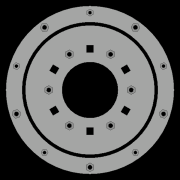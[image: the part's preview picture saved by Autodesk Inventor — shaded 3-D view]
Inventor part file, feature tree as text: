
AUTODESK INVENTOR PART (.ipt)
format: ipt  version: 2022.2 (Build 262287010, 287A)  size: 832,512 bytes
history: native  units: mm
features: extrude x28, other x19, sketch x17, pattern_circular x11, plane x4, fillet x2, move_body x2, revolve x2, draft x2, chamfer x2
ambient origin geometry x8: Origin, YZ Plane, XZ Plane, XY Plane, X Axis, Y Axis, Z Axis, Center Point
bodies: Solid5 (feature_tree)
feature tree (89):
  other  "CrossSection1"
  sketch  "Sketch7"  dims[d167=8.972256mm]
  other  "Roller1"
  other  "Roller2"
  sketch  "Sketch22"  dims[d173=10.814812mm]
  sketch  "Sketch2"  dims[d57=4.025mm d90=61.984365mm]
  sketch  "Sketch23"  dims[d201=75.0mm d232=0.0mm d233=3600.0mm]
  other  "RevRoller1"
  fillet  "Fillet1"  Radius=59.246882mm
  extrude  "Extrusion39"  Depth=61.984365mm
  pattern_circular  "Circular Pattern13"  Count=360  [1 undecoded]
  move_body  "Move Body7"
  revolve  "Revolution13"  [1 undecoded]
  fillet  "Fillet3"  Radius=0.025mm
  pattern_circular  "Circular Pattern14"  Count=24  [1 undecoded]
  move_body  "Move Body6"
  revolve  "Revolution14"  Angle=360.0deg
  other  "OuterRim_Top2"
  other  "OuterRim_Bottom2"
  plane  "Work Plane8"
  sketch  "Sketch49"  dims[d352=0.025mm]
  sketch  "Sketch50"  dims[d354=0.025mm]
  sketch  "Sketch51"  dims[d355=16.1595mm]
  extrude  "Extrusion40"  Depth=0.75mm
  extrude  "Extrusion41"  Depth=0.75mm
  extrude  "Extrusion42"  Depth=0.75mm
  extrude  "Extrusion43"  Depth=1.0mm
  sketch  "Sketch52"  dims[d356=16.159664mm]
  extrude  "Extrusion44"  Depth=0.75mm
  extrude  "Extrusion45"  TaperAngle=90.0deg  [1 undecoded]
  extrude  "Extrusion46"  Depth=0.75mm
  extrude  "Extrusion47"  Depth=0.75mm
  pattern_circular  "Circular Pattern32"  Angle=360.0deg  [1 undecoded]
  pattern_circular  "Circular Pattern33"  Angle=90.0deg  [1 undecoded]
  sketch  "Sketch57"  dims[d358=360.0deg]
  extrude  "Extrusion50"  Depth=0.1mm
  extrude  "Extrusion51"  Depth=0.75mm
  pattern_circular  "Circular Pattern34"  [2 undecoded]
  extrude  "Extrusion52"  Depth=0.75mm
  extrude  "Extrusion53"  Depth=0.75mm
  pattern_circular  "Circular Pattern35"  [2 undecoded]
  plane  "Work Plane7"
  sketch  "Sketch47"  dims[d350=47.575427mm]
  extrude  "Rotor_Ring"  TaperAngle=0.0deg  [1 undecoded]
  draft  "FaceDraft2"
  sketch  "Sketch30"  dims[d343=16.1595mm d344=16.159664mm d345=0.025mm]
  plane  "Work Plane5"
  other  "Rotor Featurs"
  other  "RotorRim_Bottom"
  extrude  "Extrusion24"  TaperAngle=0.0deg  [1 undecoded]
  extrude  "Extrusion25"  Depth=25.0mm
  extrude  "Extrusion26"  Depth=75.0mm
  pattern_circular  "Circular Pattern23"  [2 undecoded]
  sketch  "Sketch41"  dims[d347=0.1mm]
  extrude  "Extrusion27"  Depth=1.5mm
  extrude  "Extrusion28"  Depth=1.5mm
  pattern_circular  "Circular Pattern24"  [2 undecoded]
  extrude  "Extrusion29"  TaperAngle=90.0deg  [1 undecoded]
  extrude  "Extrusion30"  TaperAngle=90.0deg  [1 undecoded]
  extrude  "Extrusion31"  TaperAngle=90.0deg  [1 undecoded]
  pattern_circular  "Circular Pattern25"  [2 undecoded]
  sketch  "Sketch42"  dims[d348=0.1mm]
  extrude  "Extrusion32"  Depth=11.193516mm
  extrude  "Extrusion33"  TaperAngle=0.0deg  [1 undecoded]
  extrude  "Extrusion34"  Depth=0.75mm
  extrude  "Extrusion35"  Depth=2.0mm TaperAngle=0.0deg
  pattern_circular  "Circular Pattern26"  [2 undecoded]
  pattern_circular  "Circular Pattern27"  [2 undecoded]
  chamfer  "Chamfer1"  Distance=8.0mm
  chamfer  "Chamfer2"  Distance=2.5mm Angle=30.0deg
  draft  "FaceDraft4"
  plane  "Work Plane6"
  sketch  "Sketch43"  dims[d349=47.575591mm]
  extrude  "Extrusion37"  Depth=0.75mm
  extrude  "Extrusion38"  Depth=0.75mm TaperAngle=30.0deg
  other  "2D Equation Curve1"
  sketch  "Sketch40"  dims[d346=0.025mm]
  other  "Work Axis6"
  other  "Work Axis7"
  other  "Work Axis8"
  other  "Work Axis9"
  other  "Work Axis10"
  other  "Work Point1"
  other  "Work Point2"
  other  "Work Point3"
  other  "Work Point4"
  other  "Work Point5"
  sketch  "Sketch48"  dims[d351=0.025mm]
  sketch  "Sketch58"  dims[d359=0.5mm d360=240.0mm d361=360.0deg d363=1.308997mm d367=8.1mm d370=0.025mm d371=1.0mm d372=1.308997mm d373=90.0deg d374=0.5mm d375=240.0mm d376=360.0deg d378=90.0deg d379=0.1mm d380=0.025mm d381=0.025mm d382=0.025mm d383=0.025mm d384=11.193516mm d385=0.0mm d386=0.0mm d391=25.0mm d392=75.0mm d393=1.5mm d394=1.5mm d395=1.5mm d396=1.5mm d397=90.0deg d398=90.0deg d399=90.0deg d400=75.0mm d401=11.193516mm d402=0.0mm d486=0.436332mm d487=0.5mm d488=2.0mm d489=0.0mm d490=20.0mm d495=2.5mm d496=8.0mm d506=13.856406mm d507=55.5mm d508=8.0mm d509=0.05mm d510=2.5mm d511=30.0deg d512=12.0mm d513=6.0mm d514=0.2mm d515=30.0deg d516=131.0mm d517=65.5mm d518=0.2mm d519=100.0mm d520=120.0mm d521=2.0mm d522=150.0mm d530=50.0mm d531=5.5mm d532=5.5mm d533=5.5mm d534=85.75mm d535=73.5mm d536=61.25mm d537=24.5mm d538=3.0mm d539=2.4mm d540=0.0mm d541=0.0mm d542=0.0mm d543=5.5mm d544=3.0mm d545=0.0mm d546=90.0mm d547=360.0deg d549=3.0mm d550=3.0mm d551=2.4mm d552=0.0mm d553=5.596758mm d554=0.0mm d555=2.4mm d556=0.0mm d557=5.596758mm d558=0.0mm d559=5.596758mm d560=0.0mm d561=90.0mm d562=360.0deg d564=60.0mm d565=360.0deg d567=5.5mm d568=5.5mm d569=3.0mm d570=0.0mm d571=5.596758mm d572=0.0mm d573=3.0mm d574=0.0mm d575=5.596758mm d576=0.0mm d577=90.0mm d578=360.0deg d580=60.0mm d581=360.0deg d584=20.0mm d585=8.0mm d587=1.75mm d589=3.0mm d592=2.0mm d593=12.0mm d594=12.0mm d600=0.5mm d601=2.0mm d602=45.0deg d603=0.5mm d604=2.0mm d605=45.0deg d606=0.436332mm d607=0.5mm d608=0.0mm d609=20.0mm d611=360.0deg d613=0.0mm d614=0.0mm d617=0.99971mm d618=100.0mm d620=69.0mm d621=5.0mm d622=0.5mm d623=0.5mm d624=5.0mm d625=0.2mm d626=0.0mm d627=20.0mm d629=69.0mm d630=73.5mm d631=20.0mm d633=6.283185mm d635=5.5mm d636=3.0mm d637=7.0mm d638=4.0mm d639=5.596758mm d640=0.0mm d641=3.0mm d642=0.0mm d643=5.596758mm d644=0.0mm d645=4.0mm d646=0.0mm d647=20.0mm d649=6.283185mm d651=3.0mm d652=4.0mm d653=20.0mm d655=6.283185mm d657=7.0mm d658=5.5mm d659=5.596758mm d660=0.0mm d661=2.593516mm d662=0.0mm d663=5.596758mm d664=0.0mm d665=3.193516mm d666=0.0mm d679=50.0mm d680=360.0deg d682=50.0mm d683=360.0deg d694=6.35mm d695=6.35mm d696=6.9mm d697=5.9mm d698=11.194mm d699=0.0mm d700=8.194mm d701=0.0mm d702=60.0mm d703=360.0deg d705=30.0deg d706=4.0mm d707=7.0mm d708=3.193516mm d709=0.0mm d710=11.193516mm d711=0.0mm d712=60.0mm d713=360.0deg d16=0.872665mm d17=0.872665mm d49=0.872665mm d50=0.872665mm d51=0.872665mm d52=0.872665mm d236=0.5mm d237=0.872665mm d238=0.5mm d239=0.872665mm d282=1.0mm d283=1.0mm d284=1.0mm d285=0.15mm d286=0.25mm d287=0.375mm d288=14.3117mm d289=0.75mm d290=20.594885mm d291=0.0625mm d292=0.75mm d293=0.375mm d405=0.5mm d406=0.872665mm d407=0.5mm d408=0.872665mm d413=0.5mm d414=0.872665mm d415=0.5mm d416=0.872665mm d417=0.5mm d418=0.872665mm d419=0.5mm d420=0.872665mm d421=0.872665mm d431=0.5mm d432=0.872665mm d433=0.5mm d434=0.872665mm d471=0.5mm d472=0.872665mm d473=0.5mm d474=0.872665mm d497=0.5mm d498=0.872665mm d499=0.5mm d500=0.872665mm d590=0.5mm d591=0.872665mm]
note: 26 required parameter values undecoded (feature->parameter linkage not recoverable at this tier; creation-order binding heuristic only, values carry confidence <= 0.55)